# Revit family: Im-Beton-Kanalsystem_IBK_Im-Beton-Dose_für_GES9
name_source: partatom
category: Generic Models
revit_build: Autodesk Revit 2015 (Build: 20140606_1530(x64)
units: mm (PartAtom-declared; Revit-internal decimal feet)

## types (2) — shared parameters
Aufnahme width = 249 mm  [stored 0.816929 ft]
Manufacturer = OBO Bettermann
Material = Steel, Galvanized
URL = http://www.obo-bettermann.com
Width = 440 mm  [stored 1.44357 ft]

## per-type parameters (varying)
| type | Dose Height | GTIN | Height | Manufacturer Art. No. |
| IBD 35038 9 | 62 mm  [stored 0.203412 ft] | 4012196331734 | 142 mm | 7399850 |
| IBD 35048 9 | 72 mm  [stored 0.23622 ft] | 4012196331741
4012196331741 | 152 mm | 7399852 |

note: column(s) folded — value = type name in every type: Article Type

note: [stored X ft] marks values corroborated as IEEE doubles in the binary element streams (Revit-internal decimal feet)

## geometry (parser evidence)
native form markers: Sweep x2
no freeform markers — native parametric forms only
